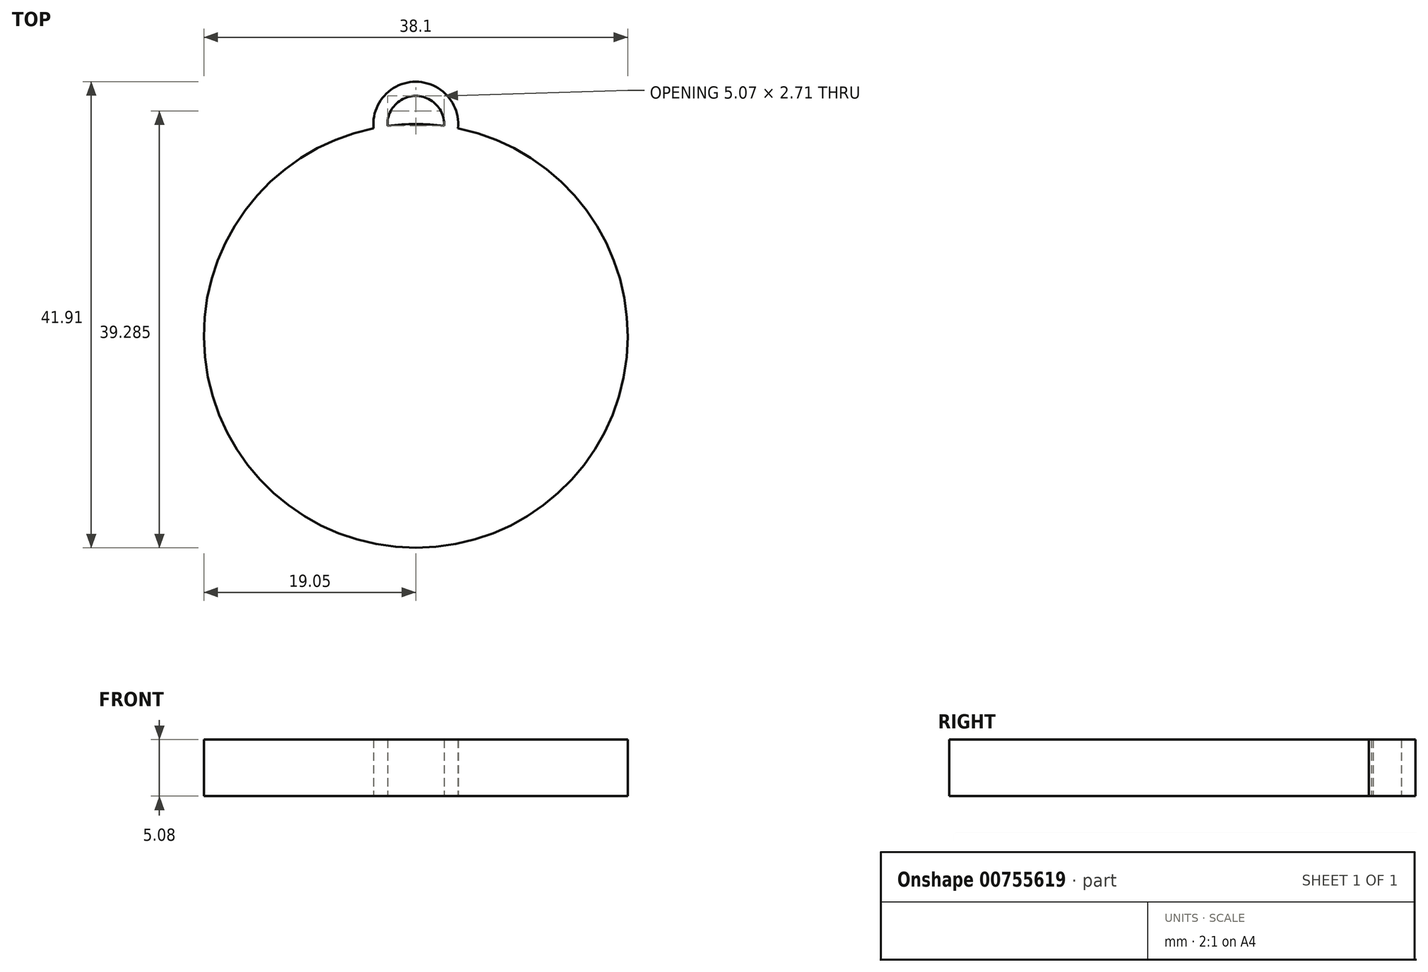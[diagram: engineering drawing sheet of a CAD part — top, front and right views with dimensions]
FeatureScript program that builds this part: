
annotation { "Feature Type Name" : "Feature", "Feature Type Description" : "" }
export const myFeature = defineFeature(function(context is Context, id is Id, definition is map)
    precondition{}
    {
        {
            var Q0;
            Q0=qCreatedBy(makeId("Top.planeOp"),FACE);
            var sketch = newSketch(context, id + "F0", { "sketchPlane" : qUnion([Q0])});
            skCircle(sketch, "E0", {"center": v(0, 0) * mm, "radius": 19.05 * mm});
            skArc(sketch, "E1", {"start": v(2.53, 18.88) * mm, "mid": v(0, 21.59) * mm, "end": v(-2.53, 18.88) * mm});
            skArc(sketch, "E2", {"start": v(3.8, 18.67) * mm, "mid": v(0, 22.86) * mm, "end": v(-3.8, 18.67) * mm});
            skSolve(sketch);
        }
        {
            var Q0;
            Q0 = qSketchRegion(id + "F0", true);
            extrude(context, id + "F1", {"entities" : qUnion([Q0]), "depth" : 5.08 * mm, "offsetDistance" : 25.4 * mm});
        }
    });
